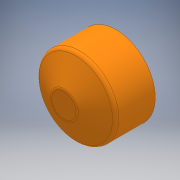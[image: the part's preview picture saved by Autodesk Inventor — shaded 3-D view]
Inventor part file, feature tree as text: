
AUTODESK INVENTOR PART (.ipt)
format: ipt  version: 2019 (Build 230136000, 136)  size: 145,408 bytes
history: native  units: mm
features: other x1, revolve x1, fillet x1, sketch x1
ambient origin geometry x8: Origin, YZ Plane, XZ Plane, XY Plane, X Axis, Y Axis, Z Axis, Center Point
bodies: Body1 (feature_tree)
feature tree (4):
  other  "Твердое тело1"
  revolve  "Вращение1"
  fillet  "Сопряжение1"  Radius=18.0mm
  sketch  "Эскиз1"
